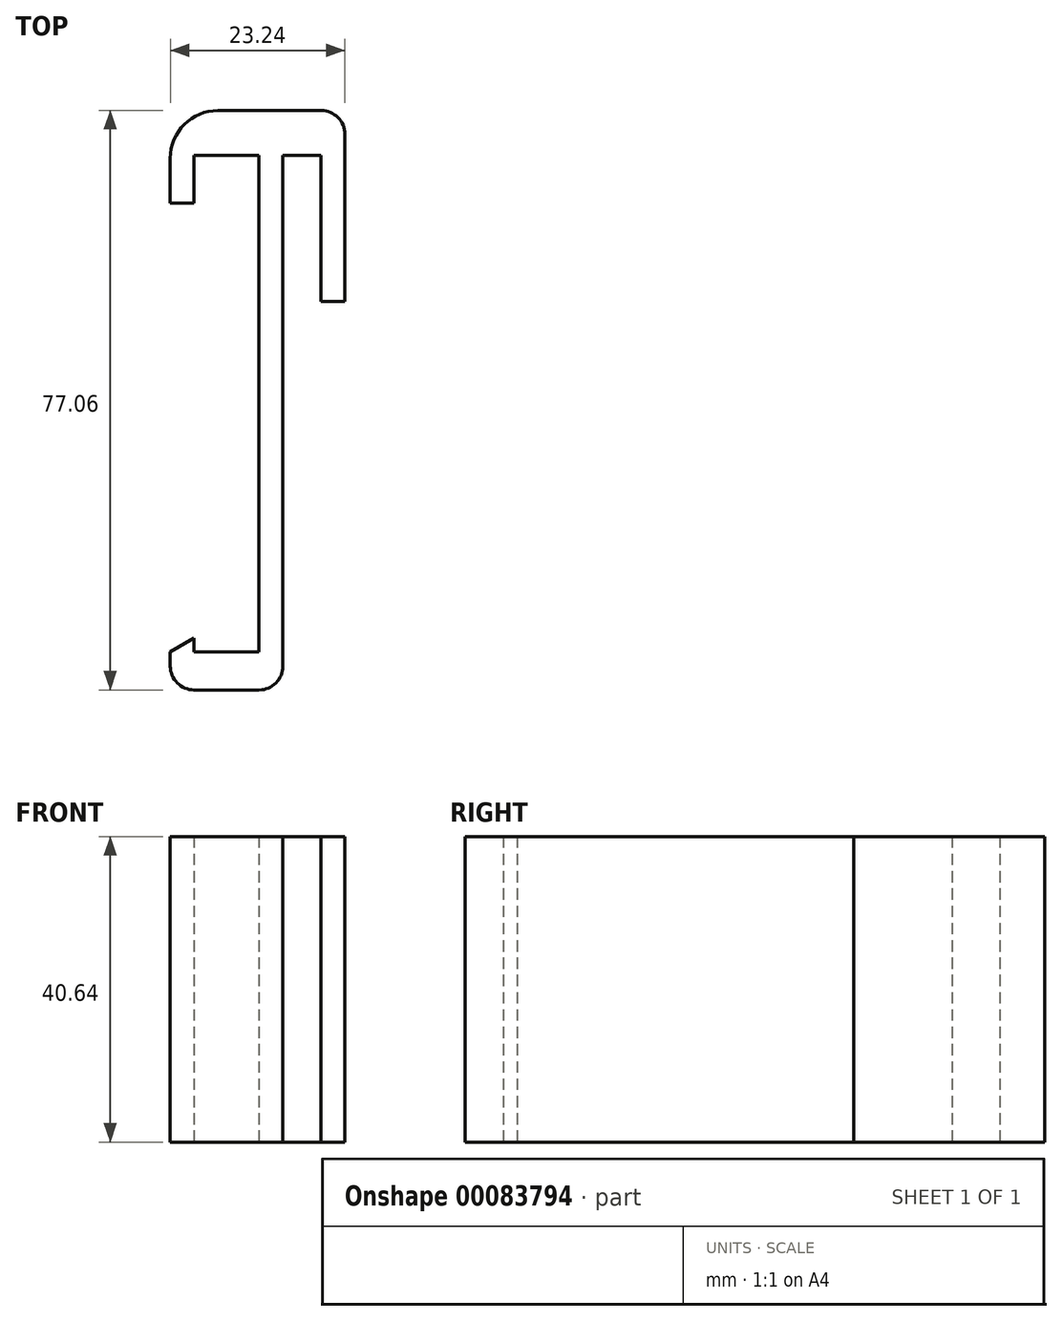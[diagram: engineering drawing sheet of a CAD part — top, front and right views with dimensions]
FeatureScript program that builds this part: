
annotation { "Feature Type Name" : "Feature", "Feature Type Description" : "" }
export const myFeature = defineFeature(function(context is Context, id is Id, definition is map)
    precondition{}
    {
        {
            var Q0;
            Q0=qCreatedBy(makeId("Top.planeOp"),FACE);
            var sketch = newSketch(context, id + "F0", { "sketchPlane" : qUnion([Q0])});
            skLineSegment(sketch, "E0", {"start": v(0, -20.45) * mm, "end": v(0, 45.59) * mm});
            skLineSegment(sketch, "E1", {"start": v(0, 45.59) * mm, "end": v(-8.64, 45.59) * mm});
            skLineSegment(sketch, "E2", {"start": v(-8.64, 45.59) * mm, "end": v(-8.64, 39.24) * mm});
            skLineSegment(sketch, "E3", {"start": v(-8.64, 39.24) * mm, "end": v(-11.81, 39.24) * mm});
            skLineSegment(sketch, "E4", {"start": v(-11.81, 39.24) * mm, "end": v(-11.81, 45.22) * mm});
            skLineSegment(sketch, "E5", {"start": v(-5.46, 51.57) * mm, "end": v(0, 51.57) * mm});
            skLineSegment(sketch, "E6", {"start": v(0, 51.57) * mm, "end": v(3.18, 51.57) * mm});
            skLineSegment(sketch, "E7", {"start": v(3.18, 51.57) * mm, "end": v(8.26, 51.57) * mm});
            skLineSegment(sketch, "E8", {"start": v(11.43, 48.4) * mm, "end": v(11.43, 26.17) * mm});
            skLineSegment(sketch, "E9", {"start": v(11.43, 26.17) * mm, "end": v(8.26, 26.17) * mm});
            skLineSegment(sketch, "E10", {"start": v(8.26, 26.17) * mm, "end": v(8.26, 45.59) * mm});
            skLineSegment(sketch, "E11", {"start": v(8.26, 45.59) * mm, "end": v(3.17, 45.59) * mm});
            skLineSegment(sketch, "E12", {"start": v(3.18, 45.59) * mm, "end": v(3.18, -20.45) * mm});
            skLineSegment(sketch, "E13", {"start": v(3.18, -20.45) * mm, "end": v(3.18, -22.32) * mm});
            skLineSegment(sketch, "E14", {"start": v(0, -25.5) * mm, "end": v(0, -25.5) * mm});
            skLineSegment(sketch, "E15", {"start": v(0, -25.5) * mm, "end": v(-8.64, -25.5) * mm});
            skLineSegment(sketch, "E16", {"start": v(-8.64, -25.5) * mm, "end": v(-8.64, -25.5) * mm});
            skLineSegment(sketch, "E17", {"start": v(-11.81, -22.32) * mm, "end": v(-11.81, -20.45) * mm});
            skLineSegment(sketch, "E18", {"start": v(-11.81, -20.45) * mm, "end": v(-8.64, -18.58) * mm});
            skLineSegment(sketch, "E19", {"start": v(-8.64, -18.58) * mm, "end": v(-8.64, -20.45) * mm});
            skLineSegment(sketch, "E20", {"start": v(-8.64, -20.45) * mm, "end": v(0, -20.45) * mm});
            skPoint(sketch, "E21.visualSharp", {"position": v(-11.81, 51.57) * mm});
            skArc(sketch, "E21.filletArc", {"start": v(-5.46, 51.57) * mm, "mid": v(-9.95, 49.7) * mm, "end": v(-11.81, 45.22) * mm});
            skPoint(sketch, "E22.visualSharp", {"position": v(11.43, 51.57) * mm});
            skArc(sketch, "E22.filletArc", {"start": v(11.43, 48.4) * mm, "mid": v(10.5, 50.64) * mm, "end": v(8.26, 51.57) * mm});
            skPoint(sketch, "E23.visualSharp", {"position": v(-11.81, -25.5) * mm});
            skArc(sketch, "E23.filletArc", {"start": v(-11.81, -22.32) * mm, "mid": v(-10.88, -24.56) * mm, "end": v(-8.64, -25.5) * mm});
            skPoint(sketch, "E24.visualSharp", {"position": v(3.18, -25.5) * mm});
            skArc(sketch, "E24.filletArc", {"start": v(0, -25.5) * mm, "mid": v(2.25, -24.56) * mm, "end": v(3.17, -22.32) * mm});
            skSolve(sketch);
        }
        {
            var Q0;
            Q0 = qSketchRegion(id + "F0", true);
            extrude(context, id + "F1", {"entities" : qUnion([Q0]), "depth" : 40.64 * mm});
        }
    });
